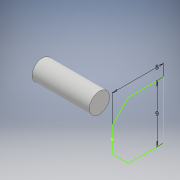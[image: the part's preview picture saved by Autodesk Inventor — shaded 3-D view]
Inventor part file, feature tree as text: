
AUTODESK INVENTOR PART (.ipt)
format: ipt  version: 2018 (Build 220112000, 112)  size: 177,664 bytes
history: native  units: mm
features: sketch x9, extrude x8, projected_geometry x1
ambient origin geometry x8: Origin, YZ Plane, XZ Plane, XY Plane, X Axis, Y Axis, Z Axis, Center Point
bodies: Solid1 (feature_tree)
feature tree (18):
  extrude  "Extrusion1"  Depth=10.0mm TaperAngle=0.0deg
  sketch  "Sketch2"  dims[d3=9.0mm d4=8.0mm d5=10.0mm d6=0.0mm]
  extrude  "Extrusion2"  Depth=10.0mm TaperAngle=0.0deg
  extrude  "Extrusion3"  Depth=1.125mm
  extrude  "Extrusion4"  Depth=1.6mm
  extrude  "Extrusion5"  Depth=1.8mm
  extrude  "Extrusion6"  Depth=2.4mm
  extrude  "Extrusion7"  Depth=3.32mm
  extrude  "Extrusion8"  Depth=10.0mm
  sketch  "Sketch1"  dims[d0=10.0mm d1=10.0mm d2=0.0mm]
  sketch  "Sketch3"  dims[d9=1.125mm d10=1.125mm]
  sketch  "Sketch4"  dims[d12=0.0mm d13=0.0mm d16=1.6mm]
  sketch  "Sketch5"  dims[d18=1.6mm d21=1.8mm]
  projected_geometry  "Projected Loop1"
  sketch  "Sketch6"  dims[d23=1.8mm d24=2.4mm]
  sketch  "Sketch7"  dims[d26=3.32mm d27=3.32mm]
  sketch  "Sketch8"  dims[d29=10.0mm d30=0.0mm d31=3.15mm]
  sketch  "Sketch9"  dims[d32=2.4mm d33=15.0mm d34=0.0mm d35=15.0mm d36=0.0mm d37=1.075mm d38=7.0mm d39=0.0mm d40=10.0mm d41=0.0mm]
